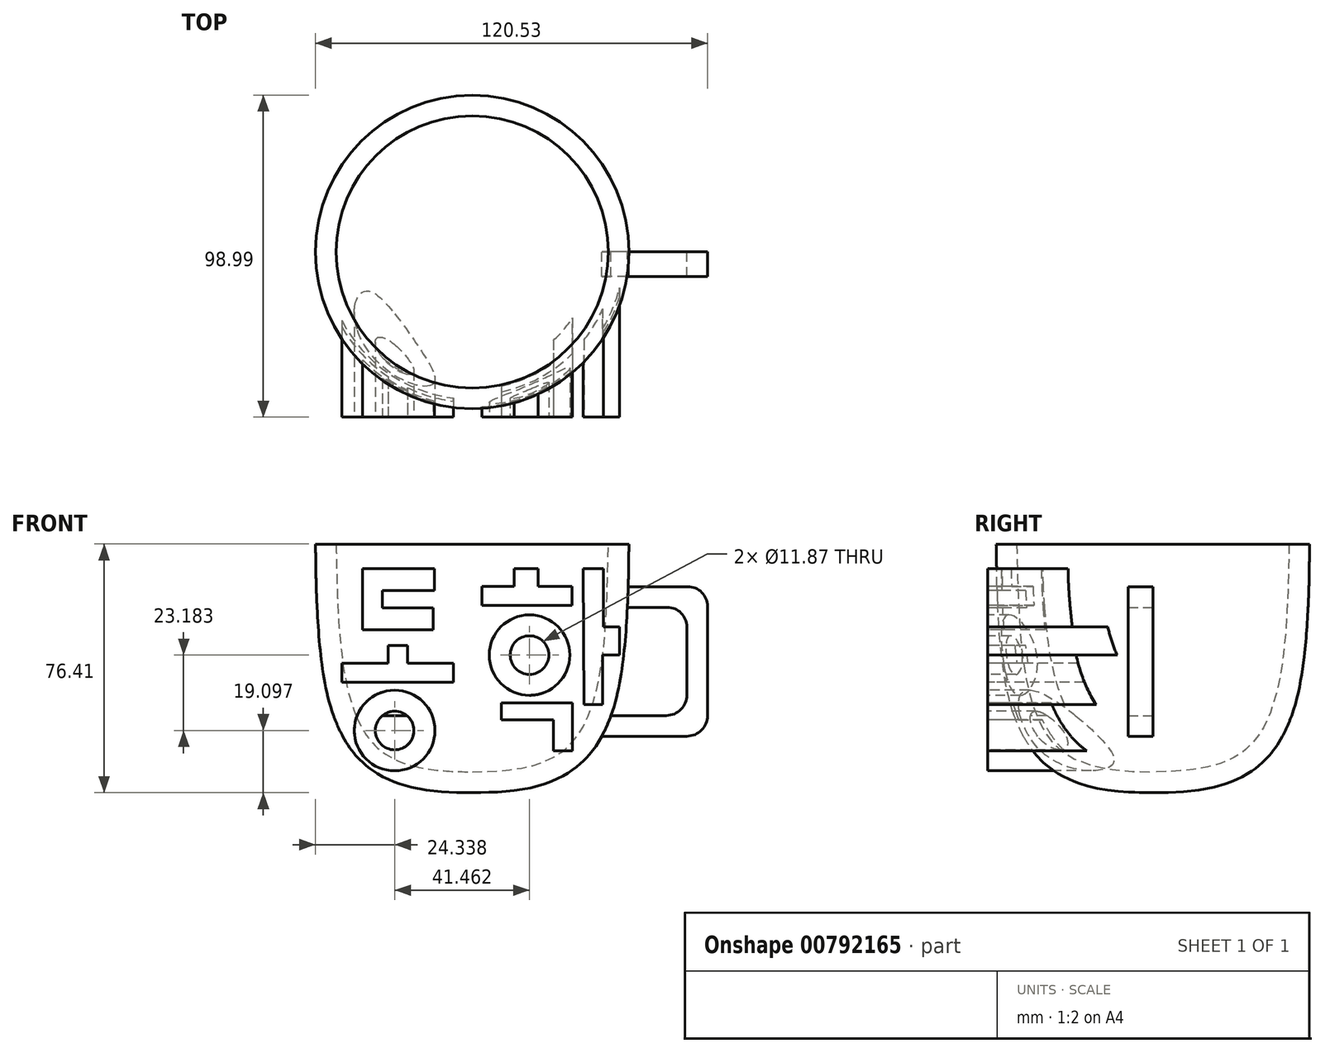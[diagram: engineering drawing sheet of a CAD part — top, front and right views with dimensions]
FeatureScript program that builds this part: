
annotation { "Feature Type Name" : "Feature", "Feature Type Description" : "" }
export const myFeature = defineFeature(function(context is Context, id is Id, definition is map)
    precondition{}
    {
        {
            var Q0;
            Q0=qCreatedBy(makeId("Front.planeOp"),FACE);
            var sketch = newSketch(context, id + "F0", { "sketchPlane" : qUnion([Q0])});
            skLineSegment(sketch, "E0", {"start": v(0, 40.7) * mm, "end": v(0, -47.26) * mm});
            skFitSpline(sketch, "E1", {"points": [v(-7.85, -35.84) * mm, v(30.13, -27.56) * mm, v(41.84, 34.13) * mm], "startDerivative": vector(100.64, -1.32) * mm, "endDerivative": vector(2.64, 135.8) * mm});
            skFitSpline(sketch, "E2.0", {"points": [v(-7.94, -42.2) * mm, v(-5.84, -42.22) * mm, v(-1.6, -42.27) * mm, v(4.82, -42.2) * mm, v(11.2, -41.8) * mm, v(17.48, -40.9) * mm, v(22.56, -39.5) * mm, v(26.48, -37.86) * mm, v(29.31, -36.33) * mm, v(31.56, -34.78) * mm, v(33.25, -33.37) * mm, v(34.47, -32.22) * mm, v(35.63, -30.99) * mm, v(37.06, -29.26) * mm, v(38.66, -26.95) * mm, v(40.3, -24) * mm, v(42.18, -19.82) * mm, v(44, -14.23) * mm, v(45.56, -7) * mm, v(46.64, 0.68) * mm, v(47.34, 8.72) * mm, v(47.9, 19.8) * mm, v(48.08, 28.35) * mm, v(48.19, 34) * mm]});
            skLineSegment(sketch, "E3", {"start": v(41.84, 34.13) * mm, "end": v(48.19, 34) * mm});
            skLineSegment(sketch, "E4", {"start": v(47.88, 21.04) * mm, "end": v(66.28, 21.04) * mm});
            skLineSegment(sketch, "E5", {"start": v(72.34, 14.97) * mm, "end": v(72.34, -18.58) * mm});
            skLineSegment(sketch, "E6", {"start": v(65.99, -24.93) * mm, "end": v(39.76, -24.93) * mm});
            skArc(sketch, "E7.filletArc", {"start": v(72.34, 14.97) * mm, "mid": v(70.56, 19.26) * mm, "end": v(66.28, 21.04) * mm});
            skArc(sketch, "E8.filletArc", {"start": v(65.99, -24.93) * mm, "mid": v(70.48, -23.07) * mm, "end": v(72.34, -18.58) * mm});
            skLineSegment(sketch, "E9.0", {"start": v(59.64, -18.58) * mm, "end": v(42.53, -18.58) * mm});
            skLineSegment(sketch, "E9.1", {"start": v(65.99, 8.62) * mm, "end": v(65.99, -12.23) * mm});
            skLineSegment(sketch, "E9.2", {"start": v(47.6, 14.69) * mm, "end": v(59.93, 14.69) * mm});
            skArc(sketch, "E10.filletArc", {"start": v(59.64, -18.58) * mm, "mid": v(64.13, -16.72) * mm, "end": v(65.99, -12.23) * mm});
            skArc(sketch, "E11.filletArc", {"start": v(65.99, 8.62) * mm, "mid": v(64.21, 12.91) * mm, "end": v(59.93, 14.69) * mm});
            skSolve(sketch);
        }
        {
            var Q0;
            {var subQ0=sQuery(id+"F0.wireOp",EDGE,"E1");Q0=makeQuery(id+"F0.imprint","IMPRINT",FACE,{"disambiguationData":[TD([[makeQuery(id+"F0.imprint","IMPRINT",EDGE,{"derivedFrom":subQ0}),-1.0]])]});}
            var Q1;
            Q1=sQuery(id+"F0.wireOp",EDGE,"E0");
            revolve(context, id + "F1", {"surfaceOperationType" : NewSurfaceOperationType.NEW, "entities" : qUnion([Q0]), "axis" : qUnion([Q1]), "revolveType" : RevolveType.FULL});
        }
        {
            var Q0;
            {var subQ0=sQuery(id+"F0.wireOp",EDGE,"E4");Q0=makeQuery(id+"F0.imprint","IMPRINT",FACE,{"disambiguationData":[TD([[makeQuery(id+"F0.imprint","IMPRINT",EDGE,{"derivedFrom":subQ0}),-1.0]])]});}
            extrude(context, id + "F2", {"entities" : qUnion([Q0]), "depth" : 7.62 * mm, "offsetDistance" : 25.4 * mm});
        }
        {
            var Q0;
            Q0=qCreatedBy(makeId("Front.planeOp"),FACE);
            cPlane(context, id + "F3", {"entities" : qUnion([Q0]), "cplaneType" : CPlaneType.OFFSET, "offset" : 50.8 * mm, "width" : 152.4 * mm, "height" : 152.4 * mm});
        }
        {
            var Q0;
            Q0=qCreatedBy(id+"F3.planeOp",FACE);
            var sketch = newSketch(context, id + "F4", { "sketchPlane" : qUnion([Q0])});
            skLineSegment(sketch, "E12", {"start": v(-33.66, 26.52) * mm, "end": v(-11.6, 26.52) * mm});
            skLineSegment(sketch, "E13", {"start": v(-11.6, 26.52) * mm, "end": v(-11.6, 19.84) * mm});
            skLineSegment(sketch, "E14", {"start": v(-11.6, 19.84) * mm, "end": v(-27.64, 19.84) * mm});
            skLineSegment(sketch, "E15", {"start": v(-27.64, 19.84) * mm, "end": v(-27.64, 14.49) * mm});
            skLineSegment(sketch, "E16", {"start": v(-27.64, 14.49) * mm, "end": v(-12.04, 14.49) * mm});
            skLineSegment(sketch, "E17", {"start": v(-25.86, 2.9) * mm, "end": v(-19.84, 2.9) * mm});
            skPoint(sketch, "E17.endSnap0", {"position": v(-19.84, 14.49) * mm});
            skLineSegment(sketch, "E18", {"start": v(-19.84, 2.9) * mm, "end": v(-19.84, -2.45) * mm});
            skLineSegment(sketch, "E19", {"start": v(-19.84, -2.45) * mm, "end": v(-5.8, -2.45) * mm});
            skLineSegment(sketch, "E20", {"start": v(-5.8, -2.45) * mm, "end": v(-5.8, -8.32) * mm});
            skLineSegment(sketch, "E21", {"start": v(-5.8, -8.32) * mm, "end": v(-40.12, -8.32) * mm});
            skLineSegment(sketch, "E22", {"start": v(-40.12, -8.32) * mm, "end": v(-40.12, -2.53) * mm});
            skLineSegment(sketch, "E23", {"start": v(-40.12, -2.53) * mm, "end": v(-25.86, -2.53) * mm});
            skLineSegment(sketch, "E24", {"start": v(-25.86, -2.53) * mm, "end": v(-25.86, 2.9) * mm});
            skLineSegment(sketch, "E25", {"start": v(12.83, 26.52) * mm, "end": v(20.28, 26.52) * mm});
            skLineSegment(sketch, "E26", {"start": v(20.28, 26.52) * mm, "end": v(20.28, 21.17) * mm});
            skLineSegment(sketch, "E27", {"start": v(20.28, 21.17) * mm, "end": v(30.67, 21.17) * mm});
            skLineSegment(sketch, "E28", {"start": v(30.67, 21.17) * mm, "end": v(30.67, 15.32) * mm});
            skLineSegment(sketch, "E29", {"start": v(30.67, 15.32) * mm, "end": v(3.03, 15.32) * mm});
            skLineSegment(sketch, "E30", {"start": v(3.03, 15.32) * mm, "end": v(3.03, 21.12) * mm});
            skLineSegment(sketch, "E31", {"start": v(3.03, 21.12) * mm, "end": v(12.83, 21.12) * mm});
            skLineSegment(sketch, "E32", {"start": v(12.83, 21.12) * mm, "end": v(12.83, 26.52) * mm});
            skLineSegment(sketch, "E33", {"start": v(34.12, 26.52) * mm, "end": v(40.35, 26.52) * mm});
            skLineSegment(sketch, "E34", {"start": v(40.35, 26.52) * mm, "end": v(40.35, 8.69) * mm});
            skLineSegment(sketch, "E35", {"start": v(40.35, 8.69) * mm, "end": v(45.25, 8.69) * mm});
            skLineSegment(sketch, "E36", {"start": v(45.25, 8.69) * mm, "end": v(45.25, 0) * mm});
            skLineSegment(sketch, "E37", {"start": v(45.25, 0) * mm, "end": v(40.12, 0) * mm});
            skLineSegment(sketch, "E38", {"start": v(40.12, 0) * mm, "end": v(40.12, -15.16) * mm});
            skLineSegment(sketch, "E39", {"start": v(40.12, -15.16) * mm, "end": v(34.33, -15.16) * mm});
            skLineSegment(sketch, "E40", {"start": v(34.33, -15.16) * mm, "end": v(34.12, 26.52) * mm});
            skLineSegment(sketch, "E41", {"start": v(8.92, -14.71) * mm, "end": v(30.82, -14.71) * mm});
            skLineSegment(sketch, "E42", {"start": v(30.82, -14.71) * mm, "end": v(30.82, -29.44) * mm});
            skLineSegment(sketch, "E43", {"start": v(30.82, -29.44) * mm, "end": v(24.97, -29.44) * mm});
            skLineSegment(sketch, "E44", {"start": v(24.97, -29.44) * mm, "end": v(24.97, -19.86) * mm});
            skLineSegment(sketch, "E45", {"start": v(24.97, -19.86) * mm, "end": v(8.92, -19.86) * mm});
            skLineSegment(sketch, "E46", {"start": v(8.92, -19.86) * mm, "end": v(8.92, -14.71) * mm});
            skLineSegment(sketch, "E47", {"start": v(-33.66, 26.52) * mm, "end": v(-33.66, 7.8) * mm});
            skLineSegment(sketch, "E48", {"start": v(-33.66, 7.8) * mm, "end": v(-12.04, 7.8) * mm});
            skLineSegment(sketch, "E49", {"start": v(-12.04, 7.8) * mm, "end": v(-12.04, 14.49) * mm});
            skCircle(sketch, "E50", {"center": v(-23.85, -23.18) * mm, "radius": 12.4 * mm});
            skCircle(sketch, "E51", {"center": v(-23.85, -23.18) * mm, "radius": 5.94 * mm});
            skCircle(sketch, "E52", {"center": v(17.6, 0) * mm, "radius": 12.36 * mm});
            skCircle(sketch, "E53", {"center": v(17.6, 0) * mm, "radius": 5.94 * mm});
            skSolve(sketch);
        }
        {
            var Q0;
            Q0=makeQuery(id+"F4.imprint","IMPRINT",FACE,{"disambiguationData":[TD([[makeQuery(id+"F4.imprint","IMPRINT",EDGE,{"derivedFrom":sQuery(id+"F4.wireOp",EDGE,"E12")}),-1.0]])]});
            var Q1;
            Q1=makeQuery(id+"F4.imprint","IMPRINT",FACE,{"disambiguationData":[TD([[makeQuery(id+"F4.imprint","IMPRINT",EDGE,{"derivedFrom":sQuery(id+"F4.wireOp",EDGE,"E17")}),-1.0]])]});
            var Q2;
            Q2=makeQuery(id+"F4.imprint","IMPRINT",FACE,{"disambiguationData":[TD([[makeQuery(id+"F4.imprint","IMPRINT",EDGE,{"derivedFrom":sQuery(id+"F4.wireOp",EDGE,"E50")}),1.0]])]});
            var Q3;
            Q3=makeQuery(id+"F4.imprint","IMPRINT",FACE,{"disambiguationData":[TD([[makeQuery(id+"F4.imprint","IMPRINT",EDGE,{"derivedFrom":sQuery(id+"F4.wireOp",EDGE,"E25")}),-1.0]])]});
            var Q4;
            Q4=makeQuery(id+"F4.imprint","IMPRINT",FACE,{"disambiguationData":[TD([[makeQuery(id+"F4.imprint","IMPRINT",EDGE,{"derivedFrom":sQuery(id+"F4.wireOp",EDGE,"E33")}),-1.0]])]});
            var Q5;
            Q5=makeQuery(id+"F4.imprint","IMPRINT",FACE,{"disambiguationData":[TD([[makeQuery(id+"F4.imprint","IMPRINT",EDGE,{"derivedFrom":sQuery(id+"F4.wireOp",EDGE,"E52")}),1.0]])]});
            var Q6;
            Q6=makeQuery(id+"F4.imprint","IMPRINT",FACE,{"disambiguationData":[TD([[makeQuery(id+"F4.imprint","IMPRINT",EDGE,{"derivedFrom":sQuery(id+"F4.wireOp",EDGE,"E41")}),-1.0]])]});
            extrude(context, id + "F5", {"entities" : qUnion([Q0, Q1, Q2, Q3, Q4, Q5, Q6]), "operationType" : NewBodyOperationType.ADD, "endBound" : BoundingType.UP_TO_NEXT, "oppositeDirection" : true, "depth" : 25.4 * mm, "offsetDistance" : 25.4 * mm});
        }
    });
